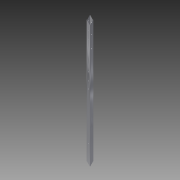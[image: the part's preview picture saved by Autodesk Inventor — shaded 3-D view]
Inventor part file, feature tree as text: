
AUTODESK INVENTOR PART (.ipt)
format: ipt  version: 2015 SP1 (Build 190203100, 203)  size: 166,400 bytes
history: native  units: in
note: dims shown in document units (in); Inventor stores cm internally (conversion verified against a paired STEP export)
features: sketch x6, hole x4, extrude x2, projected_geometry x2
ambient origin geometry x8: Origin, YZ Plane, XZ Plane, XY Plane, X Axis, Y Axis, Z Axis, Center Point
bodies: Solid1 (feature_tree)
feature tree (14):
  extrude  "Extrusion1"  Depth=1.0in
  hole  "Hole1"  [1 undecoded]
  extrude  "Extrusion2"  Depth=0.125in
  hole  "Hole5"  [1 undecoded]
  hole  "Hole6"  [1 undecoded]
  hole  "Hole10"  [1 undecoded]
  sketch  "Sketch1"  dims[d0=1.0in d1=1.0in]
  sketch  "Sketch2"  dims[d2=0.75in d3=0.75in]
  projected_geometry  "Projected Loop1"
  sketch  "Sketch3"  dims[d4=0.125in d5=0.125in]
  projected_geometry  "Projected Loop2"
  sketch  "Sketch5"  dims[d6=39.875in d7=0.0in d8=0.5in]
  sketch  "Sketch6"  dims[d9=1.5in d14=0.5in]
  sketch  "Sketch10"  dims[d15=0.5in d16=0.25in d17=0.75in d18=0.375in d19=0.25in d20=0.5635in d21=1.0in d22=0.8108in d26=1.0in d27=0.0in d57=60.0deg d58=0.5in d59=30.5in d60=0.25in d61=0.75in d62=0.375in d63=0.25in d64=0.5635in d65=1.0in d66=0.8108in d67=0.5in d68=0.5in d69=34.0in d70=37.0in d71=0.25in d72=0.75in d73=0.375in d74=0.25in d75=0.5635in d76=1.0in d77=0.8108in d114=0.5in d115=0.5in d116=35.0in d117=32.75in d118=22.5in d119=24.75in d120=0.5in d121=0.5in d122=0.5in d123=20.5in d124=7.0in d125=0.5in d126=0.25in d127=0.75in d128=0.375in d129=0.25in d130=0.5635in d131=1.0in d132=0.8108in]
note: 4 required parameter values undecoded (feature->parameter linkage not recoverable at this tier; creation-order binding heuristic only, values carry confidence <= 0.55)
